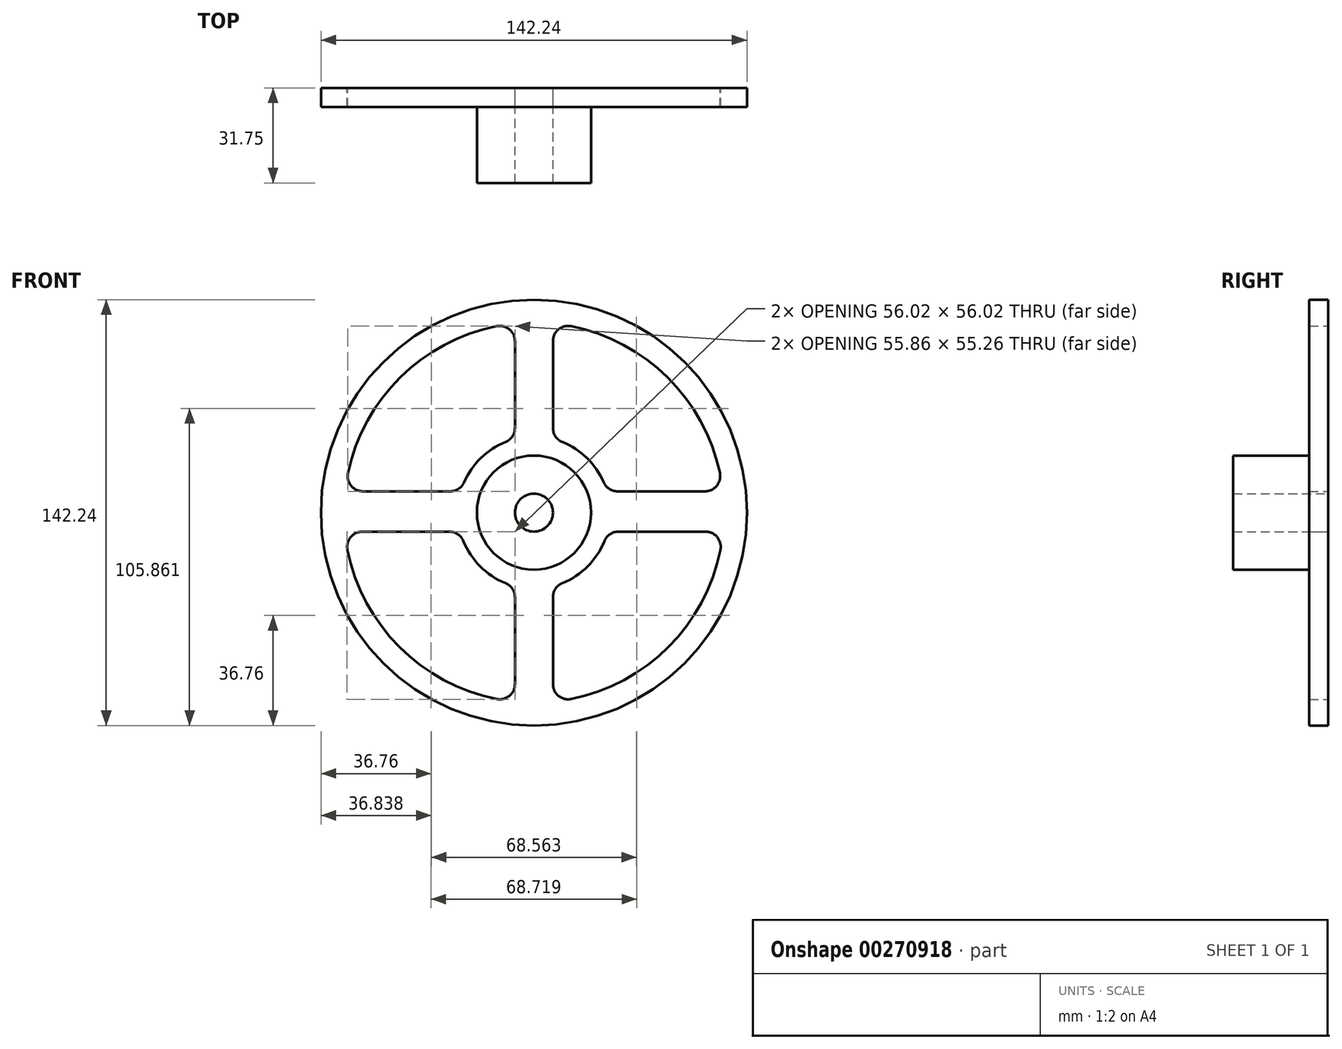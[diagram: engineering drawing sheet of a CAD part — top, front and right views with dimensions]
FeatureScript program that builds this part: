
annotation { "Feature Type Name" : "Feature", "Feature Type Description" : "" }
export const myFeature = defineFeature(function(context is Context, id is Id, definition is map)
    precondition{}
    {
        {
            var Q0;
            Q0=qCreatedBy(makeId("Front.planeOp"),FACE);
            var sketch = newSketch(context, id + "F0", { "sketchPlane" : qUnion([Q0])});
            skArc(sketch, "E0", {"start": v(-23.55, -9.53) * mm, "mid": v(-17.96, -17.96) * mm, "end": v(-9.52, -23.55) * mm});
            skCircle(sketch, "E1", {"center": v(0, 0) * mm, "radius": 6.35 * mm});
            skPoint(sketch, "E2.orphan", {"position": v(71.12, -7.43) * mm});
            skCircle(sketch, "E3", {"center": v(0, 0) * mm, "radius": 71.12 * mm});
            skLineSegment(sketch, "E4.trimOffspring", {"start": v(-6.35, -28.26) * mm, "end": v(-6.35, -57.3) * mm});
            skLineSegment(sketch, "E5.trimOffspring", {"start": v(6.35, -28.26) * mm, "end": v(6.35, -57.3) * mm});
            skLineSegment(sketch, "E6.trimOffspring", {"start": v(28.26, -6.35) * mm, "end": v(57.3, -6.35) * mm});
            skLineSegment(sketch, "E7.trimOffspring", {"start": v(27.94, 7.11) * mm, "end": v(57.13, 7.11) * mm});
            skArc(sketch, "E8.trimOffspring", {"start": v(-9.53, 23.55) * mm, "mid": v(-17.72, 18.2) * mm, "end": v(-23.28, 10.16) * mm});
            skArc(sketch, "E9.trimOffspring", {"start": v(23.28, 10.16) * mm, "mid": v(17.72, 18.2) * mm, "end": v(9.53, 23.55) * mm});
            skArc(sketch, "E10.trimOffspring", {"start": v(9.53, -23.55) * mm, "mid": v(17.96, -17.96) * mm, "end": v(23.55, -9.53) * mm});
            skPoint(sketch, "E11.visualSharp", {"position": v(-24.38, 7.11) * mm});
            skArc(sketch, "E11.filletArc", {"start": v(-27.94, 7.11) * mm, "mid": v(-25.15, 7.94) * mm, "end": v(-23.28, 10.16) * mm});
            skPoint(sketch, "E12.visualSharp", {"position": v(-24.6, -6.35) * mm});
            skArc(sketch, "E12.filletArc", {"start": v(-23.55, -9.53) * mm, "mid": v(-25.42, -7.22) * mm, "end": v(-28.26, -6.35) * mm});
            skPoint(sketch, "E13.visualSharp", {"position": v(-6.35, -24.6) * mm});
            skArc(sketch, "E13.filletArc", {"start": v(-6.35, -28.26) * mm, "mid": v(-7.22, -25.42) * mm, "end": v(-9.53, -23.55) * mm});
            skPoint(sketch, "E14.visualSharp", {"position": v(6.35, -24.6) * mm});
            skArc(sketch, "E14.filletArc", {"start": v(9.53, -23.55) * mm, "mid": v(7.22, -25.42) * mm, "end": v(6.35, -28.26) * mm});
            skPoint(sketch, "E15.visualSharp", {"position": v(24.6, -6.35) * mm});
            skArc(sketch, "E15.filletArc", {"start": v(28.26, -6.35) * mm, "mid": v(25.42, -7.22) * mm, "end": v(23.55, -9.53) * mm});
            skPoint(sketch, "E16.visualSharp", {"position": v(24.38, 7.11) * mm});
            skArc(sketch, "E16.filletArc", {"start": v(23.28, 10.16) * mm, "mid": v(25.15, 7.94) * mm, "end": v(27.94, 7.11) * mm});
            skPoint(sketch, "E17.visualSharp", {"position": v(6.35, 24.6) * mm});
            skArc(sketch, "E17.filletArc", {"start": v(6.35, 28.26) * mm, "mid": v(7.22, 25.42) * mm, "end": v(9.53, 23.55) * mm});
            skPoint(sketch, "E18.visualSharp", {"position": v(-6.35, 24.6) * mm});
            skArc(sketch, "E18.filletArc", {"start": v(-9.53, 23.55) * mm, "mid": v(-7.22, 25.42) * mm, "end": v(-6.35, 28.26) * mm});
            skArc(sketch, "E19", {"start": v(-12.42, 62.27) * mm, "mid": v(-44.6, 45.2) * mm, "end": v(-62.1, 13.25) * mm});
            skLineSegment(sketch, "E20.trimOffspring", {"start": v(-6.35, 57.3) * mm, "end": v(-6.35, 28.26) * mm});
            skLineSegment(sketch, "E21.trimOffspring", {"start": v(6.35, 57.3) * mm, "end": v(6.35, 28.26) * mm});
            skArc(sketch, "E22.trimOffspring", {"start": v(62.1, 13.25) * mm, "mid": v(44.6, 45.2) * mm, "end": v(12.42, 62.27) * mm});
            skArc(sketch, "E23.trimOffspring", {"start": v(12.42, -62.27) * mm, "mid": v(44.9, -44.9) * mm, "end": v(62.27, -12.42) * mm});
            skLineSegment(sketch, "E24.trimOffspring", {"start": v(-57.13, 7.11) * mm, "end": v(-27.94, 7.11) * mm});
            skLineSegment(sketch, "E25.trimOffspring", {"start": v(-57.3, -6.35) * mm, "end": v(-28.26, -6.35) * mm});
            skArc(sketch, "E26.trimOffspring", {"start": v(-62.27, -12.42) * mm, "mid": v(-44.9, -44.9) * mm, "end": v(-12.42, -62.27) * mm});
            skPoint(sketch, "E27.visualSharp", {"position": v(-63.1, 7.11) * mm});
            skArc(sketch, "E27.filletArc", {"start": v(-62.1, 13.25) * mm, "mid": v(-61.08, 9) * mm, "end": v(-57.13, 7.11) * mm});
            skPoint(sketch, "E28.visualSharp", {"position": v(-63.18, -6.35) * mm});
            skArc(sketch, "E28.filletArc", {"start": v(-57.3, -6.35) * mm, "mid": v(-61.22, -8.2) * mm, "end": v(-62.27, -12.42) * mm});
            skPoint(sketch, "E29.visualSharp", {"position": v(-6.35, -63.18) * mm});
            skArc(sketch, "E29.filletArc", {"start": v(-12.42, -62.27) * mm, "mid": v(-8.2, -61.22) * mm, "end": v(-6.35, -57.3) * mm});
            skPoint(sketch, "E30.visualSharp", {"position": v(6.35, -63.18) * mm});
            skArc(sketch, "E30.filletArc", {"start": v(6.35, -57.3) * mm, "mid": v(8.2, -61.22) * mm, "end": v(12.42, -62.27) * mm});
            skPoint(sketch, "E31.visualSharp", {"position": v(63.18, -6.35) * mm});
            skArc(sketch, "E31.filletArc", {"start": v(62.27, -12.42) * mm, "mid": v(61.22, -8.2) * mm, "end": v(57.3, -6.35) * mm});
            skPoint(sketch, "E32.visualSharp", {"position": v(63.1, 7.11) * mm});
            skArc(sketch, "E32.filletArc", {"start": v(57.13, 7.11) * mm, "mid": v(61.08, 9) * mm, "end": v(62.1, 13.25) * mm});
            skPoint(sketch, "E33.visualSharp", {"position": v(6.35, 63.18) * mm});
            skArc(sketch, "E33.filletArc", {"start": v(12.42, 62.27) * mm, "mid": v(8.2, 61.22) * mm, "end": v(6.35, 57.3) * mm});
            skPoint(sketch, "E34.visualSharp", {"position": v(-6.35, 63.18) * mm});
            skArc(sketch, "E34.filletArc", {"start": v(-6.35, 57.3) * mm, "mid": v(-8.2, 61.22) * mm, "end": v(-12.42, 62.27) * mm});
            skSolve(sketch);
        }
        {
            var Q0;
            Q0=makeQuery(id+"F0.imprint","IMPRINT",FACE,{"disambiguationData":[TD([[makeQuery(id+"F0.imprint","IMPRINT",EDGE,{"derivedFrom":sQuery(id+"F0.wireOp",EDGE,"E0")}),1.0]])]});
            extrude(context, id + "F1", {"entities" : qUnion([Q0]), "depth" : 6.35 * mm});
        }
        {
            var Q0;
            Q0=makeQuery(id+"F1.opExtrude","CAP_FACE",FACE,{"disambiguationData":[OSD([sQuery(id+"F0.wireOp",EDGE,"E0"),sQuery(id+"F0.wireOp",EDGE,"E1"),sQuery(id+"F0.wireOp",EDGE,"E3"),sQuery(id+"F0.wireOp",EDGE,"E4.trimOffspring"),sQuery(id+"F0.wireOp",EDGE,"E5.trimOffspring"),sQuery(id+"F0.wireOp",EDGE,"E6.trimOffspring"),sQuery(id+"F0.wireOp",EDGE,"E7.trimOffspring"),sQuery(id+"F0.wireOp",EDGE,"E8.trimOffspring"),sQuery(id+"F0.wireOp",EDGE,"E9.trimOffspring"),sQuery(id+"F0.wireOp",EDGE,"E10.trimOffspring"),sQuery(id+"F0.wireOp",EDGE,"E11.filletArc"),sQuery(id+"F0.wireOp",EDGE,"E12.filletArc"),sQuery(id+"F0.wireOp",EDGE,"E13.filletArc"),sQuery(id+"F0.wireOp",EDGE,"E14.filletArc"),sQuery(id+"F0.wireOp",EDGE,"E15.filletArc"),sQuery(id+"F0.wireOp",EDGE,"E16.filletArc"),sQuery(id+"F0.wireOp",EDGE,"E17.filletArc"),sQuery(id+"F0.wireOp",EDGE,"E18.filletArc"),sQuery(id+"F0.wireOp",EDGE,"E19"),sQuery(id+"F0.wireOp",EDGE,"E20.trimOffspring"),sQuery(id+"F0.wireOp",EDGE,"E21.trimOffspring"),sQuery(id+"F0.wireOp",EDGE,"E22.trimOffspring"),sQuery(id+"F0.wireOp",EDGE,"E23.trimOffspring"),sQuery(id+"F0.wireOp",EDGE,"E24.trimOffspring"),sQuery(id+"F0.wireOp",EDGE,"E25.trimOffspring"),sQuery(id+"F0.wireOp",EDGE,"E26.trimOffspring"),sQuery(id+"F0.wireOp",EDGE,"E27.filletArc"),sQuery(id+"F0.wireOp",EDGE,"E28.filletArc"),sQuery(id+"F0.wireOp",EDGE,"E29.filletArc"),sQuery(id+"F0.wireOp",EDGE,"E30.filletArc"),sQuery(id+"F0.wireOp",EDGE,"E31.filletArc"),sQuery(id+"F0.wireOp",EDGE,"E32.filletArc"),sQuery(id+"F0.wireOp",EDGE,"E33.filletArc"),sQuery(id+"F0.wireOp",EDGE,"E34.filletArc")])],"isStart":false});
            var sketch = newSketch(context, id + "F2", { "sketchPlane" : qUnion([Q0])});
            skCircle(sketch, "E35", {"center": v(0, 0) * mm, "radius": 19.05 * mm});
            skSolve(sketch);
        }
        {
            var Q0;
            Q0=makeQuery(id+"F2.imprint","IMPRINT",FACE,{"disambiguationData":[TD([[makeQuery(id+"F2.imprint","IMPRINT",EDGE,{"derivedFrom":sQuery(id+"F2.wireOp",EDGE,"E35")}),1.0]])]});
            extrude(context, id + "F3", {"entities" : qUnion([Q0]), "operationType" : NewBodyOperationType.ADD, "depth" : 25.4 * mm});
        }
    });
